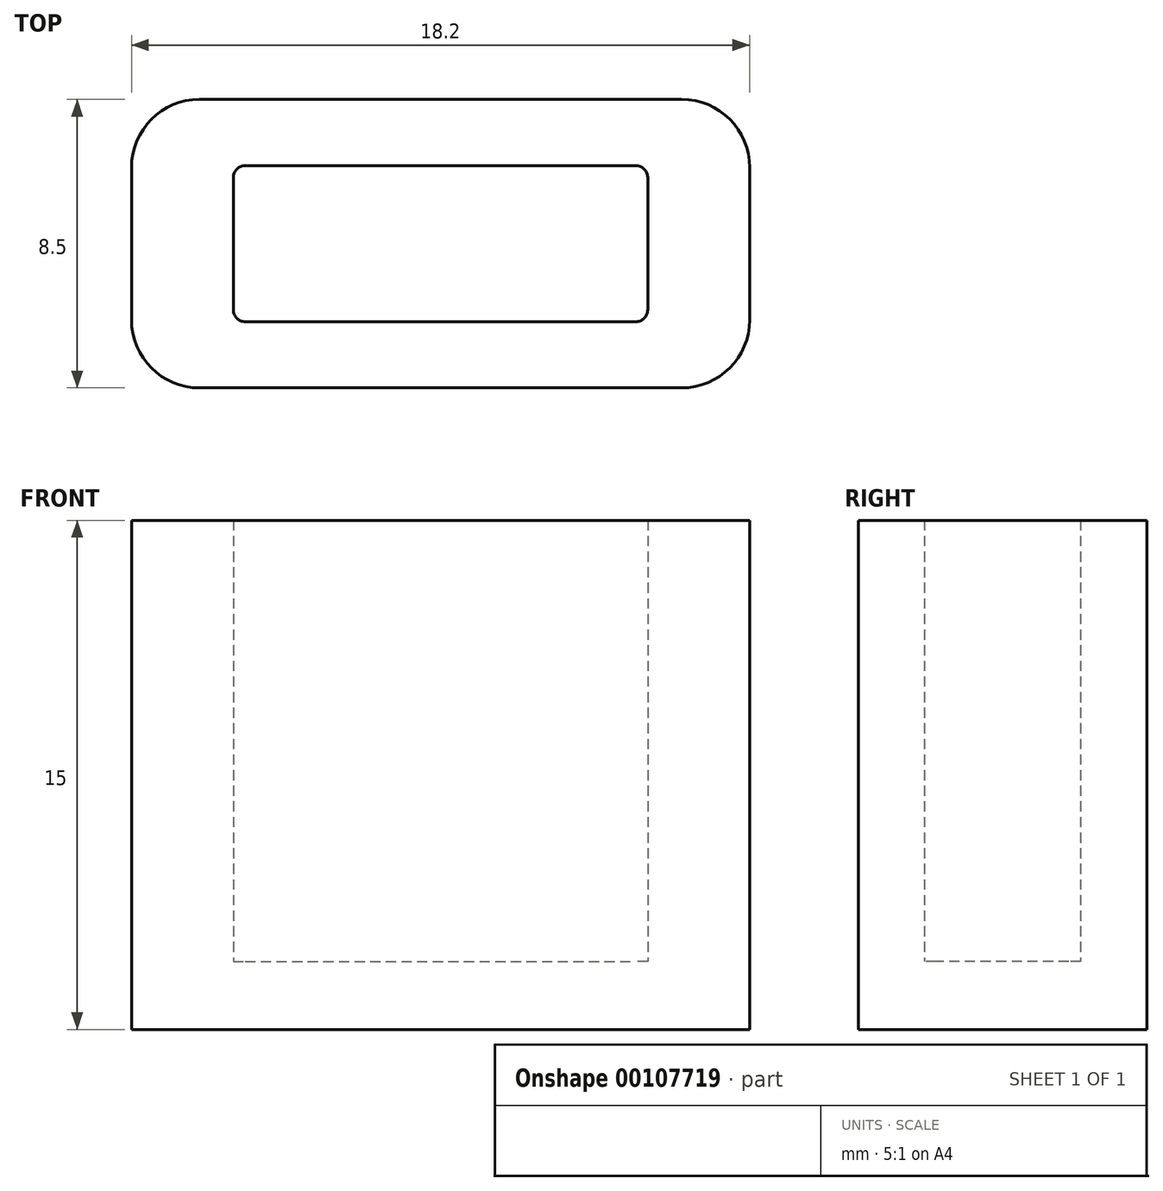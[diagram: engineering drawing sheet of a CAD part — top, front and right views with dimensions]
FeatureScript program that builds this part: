
annotation { "Feature Type Name" : "Feature", "Feature Type Description" : "" }
export const myFeature = defineFeature(function(context is Context, id is Id, definition is map)
    precondition{}
    {
        {
            var Q0;
            Q0=qCreatedBy(makeId("Top.planeOp"),FACE);
            var sketch = newSketch(context, id + "F0", { "sketchPlane" : qUnion([Q0])});
            skLineSegment(sketch, "E0.bottom", {"start": v(-6.55, 2.46) * mm, "end": v(4.95, 2.46) * mm});
            skLineSegment(sketch, "E0.top", {"start": v(-6.55, -1.94) * mm, "end": v(4.95, -1.94) * mm});
            skLineSegment(sketch, "E0.left", {"start": v(-6.8, 2.2) * mm, "end": v(-6.8, 0.56) * mm});
            skLineSegment(sketch, "E0.right", {"start": v(5.2, 2.2) * mm, "end": v(5.2, 0.56) * mm});
            skPoint(sketch, "E1.visualSharp", {"position": v(-6.8, 2.46) * mm});
            skArc(sketch, "E1.filletArc", {"start": v(-6.55, 2.46) * mm, "mid": v(-6.73, 2.39) * mm, "end": v(-6.8, 2.2) * mm});
            skPoint(sketch, "E2.visualSharp", {"position": v(-6.8, -1.94) * mm});
            skArc(sketch, "E2.filletArc", {"start": v(-6.8, -1.7) * mm, "mid": v(-6.73, -1.87) * mm, "end": v(-6.55, -1.94) * mm});
            skPoint(sketch, "E3.visualSharp", {"position": v(5.2, 2.46) * mm});
            skArc(sketch, "E3.filletArc", {"start": v(5.2, 2.2) * mm, "mid": v(5.13, 2.39) * mm, "end": v(4.95, 2.46) * mm});
            skPoint(sketch, "E4.visualSharp", {"position": v(5.2, -1.94) * mm});
            skArc(sketch, "E4.filletArc", {"start": v(4.95, -1.94) * mm, "mid": v(5.13, -1.87) * mm, "end": v(5.2, -1.7) * mm});
            skPoint(sketch, "E5", {"position": v(-6.8, 0.26) * mm});
            skPoint(sketch, "E6", {"position": v(5.2, 0.26) * mm});
            skLineSegment(sketch, "E7", {"start": v(-6.8, 0.26) * mm, "end": v(-7.85, 0.26) * mm});
            skLineSegment(sketch, "E8", {"start": v(5.2, 0.26) * mm, "end": v(6.25, 0.26) * mm});
            skLineSegment(sketch, "E9", {"start": v(-7.85, 0.26) * mm, "end": v(-7.85, 0.56) * mm});
            skLineSegment(sketch, "E10", {"start": v(-7.85, 0.56) * mm, "end": v(-6.8, 0.56) * mm});
            skLineSegment(sketch, "E11", {"start": v(-7.85, 0.26) * mm, "end": v(-7.85, -0.04) * mm});
            skLineSegment(sketch, "E12", {"start": v(-7.85, -0.04) * mm, "end": v(-6.8, -0.04) * mm});
            skLineSegment(sketch, "E13", {"start": v(6.25, 0.26) * mm, "end": v(6.25, -0.04) * mm});
            skLineSegment(sketch, "E14", {"start": v(6.25, -0.04) * mm, "end": v(5.2, -0.04) * mm});
            skLineSegment(sketch, "E15", {"start": v(6.25, 0.26) * mm, "end": v(6.25, 0.56) * mm});
            skLineSegment(sketch, "E16", {"start": v(6.25, 0.56) * mm, "end": v(5.2, 0.56) * mm});
            skPoint(sketch, "E17.end.orphan", {"position": v(-7.85, 2.46) * mm});
            skPoint(sketch, "E18.orphan", {"position": v(-7.85, -1.94) * mm});
            skPoint(sketch, "E19.end.orphan", {"position": v(6.25, 2.46) * mm});
            skPoint(sketch, "E20.orphan", {"position": v(6.25, -1.94) * mm});
            skLineSegment(sketch, "E21", {"start": v(-6.8, 0.56) * mm, "end": v(-6.8, -0.04) * mm});
            skLineSegment(sketch, "E22", {"start": v(-6.8, -0.04) * mm, "end": v(-6.8, -1.7) * mm});
            skLineSegment(sketch, "E23", {"start": v(5.2, -0.04) * mm, "end": v(5.2, -1.7) * mm});
            skLineSegment(sketch, "E24", {"start": v(5.2, 0.56) * mm, "end": v(5.2, -0.04) * mm});
            skArc(sketch, "E25.0", {"start": v(-6.55, 3.26) * mm, "mid": v(-7.3, 2.95) * mm, "end": v(-7.6, 2.2) * mm});
            skLineSegment(sketch, "E25.1", {"start": v(-6.55, 3.26) * mm, "end": v(4.95, 3.26) * mm});
            skArc(sketch, "E25.2", {"start": v(6, 2.2) * mm, "mid": v(5.7, 2.95) * mm, "end": v(4.95, 3.26) * mm});
            skLineSegment(sketch, "E25.3", {"start": v(6, 2.2) * mm, "end": v(6, 1.36) * mm});
            skLineSegment(sketch, "E25.4", {"start": v(7.05, 1.36) * mm, "end": v(6, 1.36) * mm});
            skLineSegment(sketch, "E25.5", {"start": v(-7.6, 2.2) * mm, "end": v(-7.6, 1.36) * mm});
            skLineSegment(sketch, "E25.6", {"start": v(7.05, 0.36) * mm, "end": v(7.05, 1.36) * mm});
            skLineSegment(sketch, "E25.7", {"start": v(7.05, 0.36) * mm, "end": v(7.05, -0.84) * mm});
            skLineSegment(sketch, "E25.8", {"start": v(-8.65, -0.84) * mm, "end": v(-7.6, -0.84) * mm});
            skLineSegment(sketch, "E25.9", {"start": v(-8.65, 0.36) * mm, "end": v(-8.65, -0.84) * mm});
            skLineSegment(sketch, "E25.10", {"start": v(-8.65, 0.36) * mm, "end": v(-8.65, 1.36) * mm});
            skLineSegment(sketch, "E25.11", {"start": v(-8.65, 1.36) * mm, "end": v(-7.6, 1.36) * mm});
            skLineSegment(sketch, "E25.12", {"start": v(-7.6, -0.84) * mm, "end": v(-7.6, -1.7) * mm});
            skArc(sketch, "E25.13", {"start": v(-7.6, -1.7) * mm, "mid": v(-7.3, -2.43) * mm, "end": v(-6.55, -2.74) * mm});
            skLineSegment(sketch, "E25.14", {"start": v(-6.55, -2.74) * mm, "end": v(4.95, -2.74) * mm});
            skArc(sketch, "E25.15", {"start": v(4.95, -2.74) * mm, "mid": v(5.7, -2.43) * mm, "end": v(6, -1.7) * mm});
            skLineSegment(sketch, "E25.16", {"start": v(6, -0.84) * mm, "end": v(6, -1.7) * mm});
            skLineSegment(sketch, "E25.17", {"start": v(7.05, -0.84) * mm, "end": v(6, -0.84) * mm});
            skLineSegment(sketch, "E26.0", {"start": v(-7.9, -4) * mm, "end": v(6.3, -4) * mm});
            skLineSegment(sketch, "E27.0", {"start": v(-7.9, 4.5) * mm, "end": v(6.3, 4.5) * mm});
            skLineSegment(sketch, "E28.0", {"start": v(-9.9, -2) * mm, "end": v(-9.9, 2.5) * mm});
            skLineSegment(sketch, "E29.0", {"start": v(8.3, -2) * mm, "end": v(8.3, 2.5) * mm});
            skPoint(sketch, "E30.visualSharp", {"position": v(-9.9, 4.5) * mm});
            skArc(sketch, "E30.filletArc", {"start": v(-7.9, 4.5) * mm, "mid": v(-9.31, 3.92) * mm, "end": v(-9.9, 2.5) * mm});
            skPoint(sketch, "E31.visualSharp", {"position": v(-9.9, -4) * mm});
            skArc(sketch, "E31.filletArc", {"start": v(-9.9, -2) * mm, "mid": v(-9.31, -3.4) * mm, "end": v(-7.9, -4) * mm});
            skPoint(sketch, "E32.visualSharp", {"position": v(8.3, -4) * mm});
            skArc(sketch, "E32.filletArc", {"start": v(6.3, -4) * mm, "mid": v(7.71, -3.4) * mm, "end": v(8.3, -2) * mm});
            skPoint(sketch, "E33.visualSharp", {"position": v(8.3, 4.5) * mm});
            skArc(sketch, "E33.filletArc", {"start": v(8.3, 2.5) * mm, "mid": v(7.71, 3.92) * mm, "end": v(6.3, 4.5) * mm});
            skLineSegment(sketch, "E34", {"start": v(-7.6, 1.36) * mm, "end": v(-7.6, -0.84) * mm});
            skLineSegment(sketch, "E35", {"start": v(6, 1.36) * mm, "end": v(6, -0.84) * mm});
            skArc(sketch, "E36.0", {"start": v(-6.9, -1.7) * mm, "mid": v(-6.8, -1.94) * mm, "end": v(-6.55, -2.04) * mm});
            skLineSegment(sketch, "E36.1", {"start": v(5.3, 2.2) * mm, "end": v(5.3, 0.76) * mm});
            skLineSegment(sketch, "E36.2", {"start": v(5.3, 0.76) * mm, "end": v(5.3, -0.04) * mm});
            skLineSegment(sketch, "E36.3", {"start": v(5.3, -0.04) * mm, "end": v(5.3, -1.7) * mm});
            skArc(sketch, "E36.4", {"start": v(4.95, -2.04) * mm, "mid": v(5.2, -1.94) * mm, "end": v(5.3, -1.7) * mm});
            skArc(sketch, "E36.5", {"start": v(5.3, 2.2) * mm, "mid": v(5.2, 2.46) * mm, "end": v(4.95, 2.56) * mm});
            skLineSegment(sketch, "E36.6", {"start": v(-6.55, -2.04) * mm, "end": v(4.95, -2.04) * mm});
            skLineSegment(sketch, "E36.7", {"start": v(-6.55, 2.56) * mm, "end": v(4.95, 2.56) * mm});
            skArc(sketch, "E36.8", {"start": v(-6.55, 2.56) * mm, "mid": v(-6.8, 2.46) * mm, "end": v(-6.9, 2.2) * mm});
            skLineSegment(sketch, "E36.9", {"start": v(-6.9, 2.2) * mm, "end": v(-6.9, 0.76) * mm});
            skLineSegment(sketch, "E36.10", {"start": v(-6.9, 0.76) * mm, "end": v(-6.9, -0.04) * mm});
            skLineSegment(sketch, "E36.11", {"start": v(-6.9, -0.04) * mm, "end": v(-6.9, -1.7) * mm});
            skSolve(sketch);
        }
        {
            var Q0;
            Q0=makeQuery(id+"F0.imprint","IMPRINT",FACE,{"disambiguationData":[TD([[makeQuery(id+"F0.imprint","IMPRINT",EDGE,{"derivedFrom":sQuery(id+"F0.wireOp",EDGE,"E25.0")}),-1.0]])]});
            var Q1;
            Q1=makeQuery(id+"F0.imprint","IMPRINT",FACE,{"disambiguationData":[TD([[makeQuery(id+"F0.imprint","IMPRINT",EDGE,{"derivedFrom":sQuery(id+"F0.wireOp",EDGE,"E25.0")}),1.0]])]});
            var Q2;
            {var subQ4=sQuery(id+"F0.wireOp",EDGE,"E9");Q2=makeQuery(id+"F0.imprint","IMPRINT",FACE,{"disambiguationData":[TD([[makeQuery(id+"F0.imprint","IMPRINT",EDGE,{"derivedFrom":subQ4}),1.0]])]});}
            var Q3;
            {var subQ0=sQuery(id+"F0.wireOp",EDGE,"E36.10");var subQ1=sQuery(id+"F0.wireOp",EDGE,"E7");var subQ2=makeQuery(id+"F0.imprint","INTERSECT",VERTEX,{"derivedFrom":[subQ1,subQ0]});Q3=makeQuery(id+"F0.imprint","IMPRINT",FACE,{"disambiguationData":[TD([[makeQuery(id+"F0.imprint","IMPRINT",EDGE,{"disambiguationData":[TD([[subQ2,-1.0]])],"derivedFrom":subQ1}),-1.0]])]});}
            var Q4;
            {var subQ0=sQuery(id+"F0.wireOp",EDGE,"E9");Q4=makeQuery(id+"F0.imprint","IMPRINT",FACE,{"disambiguationData":[TD([[makeQuery(id+"F0.imprint","IMPRINT",EDGE,{"derivedFrom":subQ0}),-1.0]])]});}
            var Q5;
            {var subQ0=sQuery(id+"F0.wireOp",EDGE,"E36.10");var subQ1=sQuery(id+"F0.wireOp",EDGE,"E7");var subQ2=makeQuery(id+"F0.imprint","INTERSECT",VERTEX,{"derivedFrom":[subQ1,subQ0]});Q5=makeQuery(id+"F0.imprint","IMPRINT",FACE,{"disambiguationData":[TD([[makeQuery(id+"F0.imprint","IMPRINT",EDGE,{"disambiguationData":[TD([[subQ2,-1.0]])],"derivedFrom":subQ1}),1.0]])]});}
            var Q6;
            {var subQ1=sQuery(id+"F0.wireOp",EDGE,"E25.12");Q6=makeQuery(id+"F0.imprint","IMPRINT",FACE,{"disambiguationData":[TD([[makeQuery(id+"F0.imprint","IMPRINT",EDGE,{"derivedFrom":subQ1}),1.0]])]});}
            var Q7;
            {var subQ0=sQuery(id+"F0.wireOp",EDGE,"E36.2");var subQ1=sQuery(id+"F0.wireOp",EDGE,"E8");var subQ2=makeQuery(id+"F0.imprint","INTERSECT",VERTEX,{"derivedFrom":[subQ1,subQ0]});Q7=makeQuery(id+"F0.imprint","IMPRINT",FACE,{"disambiguationData":[TD([[makeQuery(id+"F0.imprint","IMPRINT",EDGE,{"disambiguationData":[TD([[subQ2,-1.0]])],"derivedFrom":subQ1}),-1.0]])]});}
            var Q8;
            {var subQ0=sQuery(id+"F0.wireOp",EDGE,"E36.2");var subQ1=sQuery(id+"F0.wireOp",EDGE,"E8");var subQ2=makeQuery(id+"F0.imprint","INTERSECT",VERTEX,{"derivedFrom":[subQ1,subQ0]});Q8=makeQuery(id+"F0.imprint","IMPRINT",FACE,{"disambiguationData":[TD([[makeQuery(id+"F0.imprint","IMPRINT",EDGE,{"disambiguationData":[TD([[subQ2,-1.0]])],"derivedFrom":subQ1}),1.0]])]});}
            var Q9;
            {var subQ5=sQuery(id+"F0.wireOp",EDGE,"E13");Q9=makeQuery(id+"F0.imprint","IMPRINT",FACE,{"disambiguationData":[TD([[makeQuery(id+"F0.imprint","IMPRINT",EDGE,{"derivedFrom":subQ5}),1.0]])]});}
            var Q10;
            {var subQ0=sQuery(id+"F0.wireOp",EDGE,"E15");Q10=makeQuery(id+"F0.imprint","IMPRINT",FACE,{"disambiguationData":[TD([[makeQuery(id+"F0.imprint","IMPRINT",EDGE,{"derivedFrom":subQ0}),1.0]])]});}
            var Q11;
            {var subQ0=sQuery(id+"F0.wireOp",EDGE,"E13");Q11=makeQuery(id+"F0.imprint","IMPRINT",FACE,{"disambiguationData":[TD([[makeQuery(id+"F0.imprint","IMPRINT",EDGE,{"derivedFrom":subQ0}),-1.0]])]});}
            var Q12;
            {var subQ0=sQuery(id+"F0.wireOp",EDGE,"E11");Q12=makeQuery(id+"F0.imprint","IMPRINT",FACE,{"disambiguationData":[TD([[makeQuery(id+"F0.imprint","IMPRINT",EDGE,{"derivedFrom":subQ0}),1.0]])]});}
            extrude(context, id + "F1", {"entities" : qUnion([Q0, Q1, Q2, Q3, Q4, Q5, Q6, Q7, Q8, Q9, Q10, Q11, Q12]), "depth" : 13 * mm});
        }
        {
            var Q0;
            {var subQ4=sQuery(id+"F0.wireOp",EDGE,"E9");Q0=makeQuery(id+"F0.imprint","IMPRINT",FACE,{"disambiguationData":[TD([[makeQuery(id+"F0.imprint","IMPRINT",EDGE,{"derivedFrom":subQ4}),1.0]])]});}
            var Q1;
            Q1=makeQuery(id+"F0.imprint","IMPRINT",FACE,{"disambiguationData":[TD([[makeQuery(id+"F0.imprint","IMPRINT",EDGE,{"derivedFrom":sQuery(id+"F0.wireOp",EDGE,"E25.0")}),-1.0]])]});
            var Q2;
            {var subQ0=sQuery(id+"F0.wireOp",EDGE,"E36.2");var subQ1=sQuery(id+"F0.wireOp",EDGE,"E8");var subQ2=makeQuery(id+"F0.imprint","INTERSECT",VERTEX,{"derivedFrom":[subQ1,subQ0]});Q2=makeQuery(id+"F0.imprint","IMPRINT",FACE,{"disambiguationData":[TD([[makeQuery(id+"F0.imprint","IMPRINT",EDGE,{"disambiguationData":[TD([[subQ2,-1.0]])],"derivedFrom":subQ1}),-1.0]])]});}
            var Q3;
            {var subQ0=sQuery(id+"F0.wireOp",EDGE,"E36.10");var subQ1=sQuery(id+"F0.wireOp",EDGE,"E7");var subQ2=makeQuery(id+"F0.imprint","INTERSECT",VERTEX,{"derivedFrom":[subQ1,subQ0]});Q3=makeQuery(id+"F0.imprint","IMPRINT",FACE,{"disambiguationData":[TD([[makeQuery(id+"F0.imprint","IMPRINT",EDGE,{"disambiguationData":[TD([[subQ2,-1.0]])],"derivedFrom":subQ1}),1.0]])]});}
            var Q4;
            {var subQ0=sQuery(id+"F0.wireOp",EDGE,"E36.10");var subQ1=sQuery(id+"F0.wireOp",EDGE,"E7");var subQ2=makeQuery(id+"F0.imprint","INTERSECT",VERTEX,{"derivedFrom":[subQ1,subQ0]});Q4=makeQuery(id+"F0.imprint","IMPRINT",FACE,{"disambiguationData":[TD([[makeQuery(id+"F0.imprint","IMPRINT",EDGE,{"disambiguationData":[TD([[subQ2,-1.0]])],"derivedFrom":subQ1}),-1.0]])]});}
            var Q5;
            {var subQ5=sQuery(id+"F0.wireOp",EDGE,"E13");Q5=makeQuery(id+"F0.imprint","IMPRINT",FACE,{"disambiguationData":[TD([[makeQuery(id+"F0.imprint","IMPRINT",EDGE,{"derivedFrom":subQ5}),1.0]])]});}
            var Q6;
            {var subQ0=sQuery(id+"F0.wireOp",EDGE,"E36.2");var subQ1=sQuery(id+"F0.wireOp",EDGE,"E8");var subQ2=makeQuery(id+"F0.imprint","INTERSECT",VERTEX,{"derivedFrom":[subQ1,subQ0]});Q6=makeQuery(id+"F0.imprint","IMPRINT",FACE,{"disambiguationData":[TD([[makeQuery(id+"F0.imprint","IMPRINT",EDGE,{"disambiguationData":[TD([[subQ2,-1.0]])],"derivedFrom":subQ1}),1.0]])]});}
            var Q7;
            {var subQ1=sQuery(id+"F0.wireOp",EDGE,"E25.12");Q7=makeQuery(id+"F0.imprint","IMPRINT",FACE,{"disambiguationData":[TD([[makeQuery(id+"F0.imprint","IMPRINT",EDGE,{"derivedFrom":subQ1}),1.0]])]});}
            var Q8;
            Q8=makeQuery(id+"F0.imprint","IMPRINT",FACE,{"disambiguationData":[TD([[makeQuery(id+"F0.imprint","IMPRINT",EDGE,{"derivedFrom":sQuery(id+"F0.wireOp",EDGE,"E0.bottom")}),-1.0]])]});
            var Q9;
            Q9=makeQuery(id+"F0.imprint","IMPRINT",FACE,{"disambiguationData":[TD([[makeQuery(id+"F0.imprint","IMPRINT",EDGE,{"derivedFrom":sQuery(id+"F0.wireOp",EDGE,"E25.0")}),1.0]])]});
            var Q10;
            Q10=makeQuery(id+"F0.imprint","IMPRINT",FACE,{"disambiguationData":[TD([[makeQuery(id+"F0.imprint","IMPRINT",EDGE,{"derivedFrom":sQuery(id+"F0.wireOp",EDGE,"E0.top")}),-1.0]])]});
            var Q11;
            Q11=makeQuery(id+"F0.imprint","IMPRINT",FACE,{"disambiguationData":[TD([[makeQuery(id+"F0.imprint","IMPRINT",EDGE,{"derivedFrom":sQuery(id+"F0.wireOp",EDGE,"E0.bottom")}),1.0]])]});
            var Q12;
            {var subQ0=sQuery(id+"F0.wireOp",EDGE,"E15");Q12=makeQuery(id+"F0.imprint","IMPRINT",FACE,{"disambiguationData":[TD([[makeQuery(id+"F0.imprint","IMPRINT",EDGE,{"derivedFrom":subQ0}),1.0]])]});}
            var Q13;
            {var subQ0=sQuery(id+"F0.wireOp",EDGE,"E13");Q13=makeQuery(id+"F0.imprint","IMPRINT",FACE,{"disambiguationData":[TD([[makeQuery(id+"F0.imprint","IMPRINT",EDGE,{"derivedFrom":subQ0}),-1.0]])]});}
            var Q14;
            {var subQ0=sQuery(id+"F0.wireOp",EDGE,"E11");Q14=makeQuery(id+"F0.imprint","IMPRINT",FACE,{"disambiguationData":[TD([[makeQuery(id+"F0.imprint","IMPRINT",EDGE,{"derivedFrom":subQ0}),1.0]])]});}
            var Q15;
            {var subQ0=sQuery(id+"F0.wireOp",EDGE,"E9");Q15=makeQuery(id+"F0.imprint","IMPRINT",FACE,{"disambiguationData":[TD([[makeQuery(id+"F0.imprint","IMPRINT",EDGE,{"derivedFrom":subQ0}),-1.0]])]});}
            var Q16;
            {var subQ0=sQuery(id+"F0.wireOp",EDGE,"E24");var subQ1=sQuery(id+"F0.wireOp",EDGE,"E8");var subQ2=makeQuery(id+"F0.imprint","INTERSECT",VERTEX,{"derivedFrom":[subQ1,subQ0]});Q16=makeQuery(id+"F0.imprint","IMPRINT",FACE,{"disambiguationData":[TD([[makeQuery(id+"F0.imprint","IMPRINT",EDGE,{"disambiguationData":[TD([[subQ2,-1.0]])],"derivedFrom":subQ1}),1.0]])]});}
            var Q17;
            {var subQ0=sQuery(id+"F0.wireOp",EDGE,"E24");var subQ1=sQuery(id+"F0.wireOp",EDGE,"E8");var subQ2=makeQuery(id+"F0.imprint","INTERSECT",VERTEX,{"derivedFrom":[subQ1,subQ0]});Q17=makeQuery(id+"F0.imprint","IMPRINT",FACE,{"disambiguationData":[TD([[makeQuery(id+"F0.imprint","IMPRINT",EDGE,{"disambiguationData":[TD([[subQ2,-1.0]])],"derivedFrom":subQ1}),-1.0]])]});}
            var Q18;
            {var subQ0=sQuery(id+"F0.wireOp",EDGE,"E21");var subQ1=sQuery(id+"F0.wireOp",EDGE,"E7");var subQ2=makeQuery(id+"F0.imprint","INTERSECT",VERTEX,{"derivedFrom":[subQ1,subQ0]});Q18=makeQuery(id+"F0.imprint","IMPRINT",FACE,{"disambiguationData":[TD([[makeQuery(id+"F0.imprint","IMPRINT",EDGE,{"disambiguationData":[TD([[subQ2,-1.0]])],"derivedFrom":subQ1}),1.0]])]});}
            var Q19;
            {var subQ0=sQuery(id+"F0.wireOp",EDGE,"E21");var subQ1=sQuery(id+"F0.wireOp",EDGE,"E7");var subQ2=makeQuery(id+"F0.imprint","INTERSECT",VERTEX,{"derivedFrom":[subQ1,subQ0]});Q19=makeQuery(id+"F0.imprint","IMPRINT",FACE,{"disambiguationData":[TD([[makeQuery(id+"F0.imprint","IMPRINT",EDGE,{"disambiguationData":[TD([[subQ2,-1.0]])],"derivedFrom":subQ1}),-1.0]])]});}
            extrude(context, id + "F2", {"entities" : qUnion([Q0, Q1, Q2, Q3, Q4, Q5, Q6, Q7, Q8, Q9, Q10, Q11, Q12, Q13, Q14, Q15, Q16, Q17, Q18, Q19]), "operationType" : NewBodyOperationType.ADD, "oppositeDirection" : true, "depth" : 2 * mm});
        }
    });
